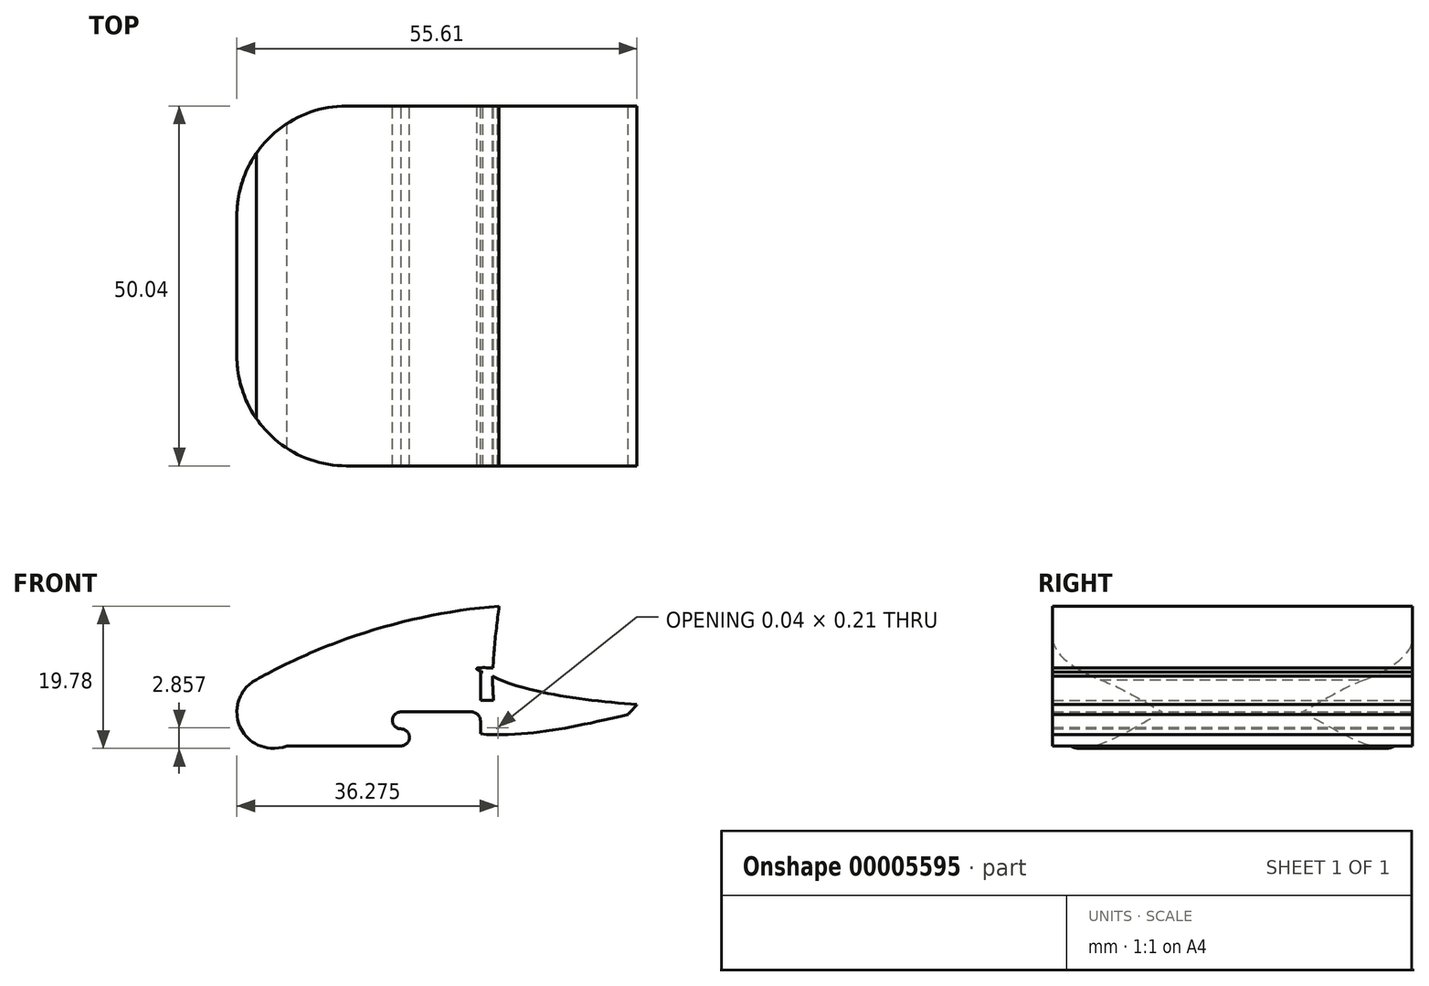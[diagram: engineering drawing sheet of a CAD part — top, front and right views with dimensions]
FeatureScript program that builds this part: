
annotation { "Feature Type Name" : "Feature", "Feature Type Description" : "" }
export const myFeature = defineFeature(function(context is Context, id is Id, definition is map)
    precondition{}
    {
        {
            var Q0;
            Q0=qCreatedBy(makeId("Top.planeOp"),FACE);
            var sketch = newSketch(context, id + "F0", { "sketchPlane" : qUnion([Q0])});
            skLineSegment(sketch, "E0.bottom", {"start": v(-7.57, 33.45) * mm, "end": v(37.92, 33.45) * mm});
            skLineSegment(sketch, "E0.top", {"start": v(-7.57, -16.6) * mm, "end": v(37.92, -16.6) * mm});
            skLineSegment(sketch, "E0.left", {"start": v(-22.81, 18.2) * mm, "end": v(-22.81, -1.35) * mm});
            skLineSegment(sketch, "E0.right", {"start": v(37.92, 33.45) * mm, "end": v(37.92, -16.6) * mm});
            skPoint(sketch, "E1.visualSharp", {"position": v(-22.81, 33.45) * mm});
            skArc(sketch, "E1.filletArc", {"start": v(-7.57, 33.45) * mm, "mid": v(-18.35, 28.98) * mm, "end": v(-22.81, 18.2) * mm});
            skPoint(sketch, "E2.visualSharp", {"position": v(-22.81, -16.6) * mm});
            skArc(sketch, "E2.filletArc", {"start": v(-22.81, -1.35) * mm, "mid": v(-18.35, -12.13) * mm, "end": v(-7.57, -16.6) * mm});
            skSolve(sketch);
        }
        {
            var Q0;
            Q0=qCreatedBy(makeId("Front.planeOp"),FACE);
            var sketch = newSketch(context, id + "F1", { "sketchPlane" : qUnion([Q0])});
            skPoint(sketch, "E3.first.point", {"position": v(-22.81, 0) * mm});
            skPoint(sketch, "E3.second.point", {"position": v(-22.81, 0) * mm});
            skLineSegment(sketch, "E4", {"start": v(-15.88, -4.73) * mm, "end": v(0, -4.73) * mm});
            skLineSegment(sketch, "E5", {"start": v(11.05, -1.27) * mm, "end": v(11.05, -5.54) * mm});
            skFitSpline(sketch, "E6", {"points": [v(11.05, -5.54) * mm, v(29.15, -2.33) * mm, v(36.06, 4.72) * mm], "startDerivative": vector(15.96, -0.07) * mm, "endDerivative": vector(7.94, 0) * mm});
            skArc(sketch, "E7", {"start": v(0, -4.73) * mm, "mid": v(1.18, -3.55) * mm, "end": v(0, -2.37) * mm});
            skArc(sketch, "E8", {"start": v(0, 0) * mm, "mid": v(-1.18, -1.19) * mm, "end": v(0, -2.37) * mm});
            skPoint(sketch, "E9.orphan", {"position": v(0, 0) * mm});
            skPoint(sketch, "E10.trimOffspring.start.orphan", {"position": v(0, -2.37) * mm});
            skLineSegment(sketch, "E11", {"start": v(0, 0) * mm, "end": v(9.78, 0) * mm});
            skPoint(sketch, "E12.visualSharp", {"position": v(11.05, 0) * mm});
            skArc(sketch, "E12.filletArc", {"start": v(11.05, -1.27) * mm, "mid": v(10.68, -0.37) * mm, "end": v(9.78, 0) * mm});
            skArc(sketch, "E13", {"start": v(11.05, -5.54) * mm, "mid": v(12.3, -6.66) * mm, "end": v(13.4, -5.38) * mm});
            skFitSpline(sketch, "E14.0", {"points": [v(8.32, -2.6) * mm, v(10, -2.92) * mm, v(12.5, -3.16) * mm, v(15.86, -3.11) * mm, v(18.41, -2.9) * mm, v(21.02, -2.55) * mm, v(23.71, -2.08) * mm, v(26.5, -1.52) * mm, v(29.4, -0.88) * mm, v(31.71, -0.3) * mm, v(33.4, 0.16) * mm, v(34.56, 0.52) * mm, v(35.58, 0.88) * mm, v(36.43, 1.23) * mm, v(36.97, 1.52) * mm, v(37.28, 1.73) * mm, v(37.44, 1.88) * mm, v(37.53, 2) * mm, v(37.56, 2.05) * mm, v(37.55, 2.05) * mm, v(37.55, 2.08) * mm, v(37.5, 2.16) * mm, v(37.39, 2.27) * mm, v(37.21, 2.4) * mm, v(36.9, 2.56) * mm, v(36.4, 2.76) * mm, v(35.68, 2.95) * mm, v(34.88, 3.08) * mm, v(34.33, 3.1) * mm, v(34.06, 3.11) * mm]});
            skArc(sketch, "E15", {"start": v(37.04, 3.92) * mm, "mid": v(37.04, 3.92) * mm, "end": v(37.04, 3.92) * mm});
            skFitSpline(sketch, "E16", {"points": [v(13.64, -3.12) * mm, v(12.75, 3.68) * mm, v(13.64, 14.7) * mm], "startDerivative": vector(-2.8, 14.5) * mm, "endDerivative": vector(2.58, 20.9) * mm});
            skArc(sketch, "E17", {"start": v(13.64, 14.7) * mm, "mid": v(-3.8, 11.4) * mm, "end": v(-20.13, 4.48) * mm});
            skArc(sketch, "E18", {"start": v(-20.13, 4.48) * mm, "mid": v(-22.34, -2.13) * mm, "end": v(-15.88, -4.73) * mm});
            skArc(sketch, "E19", {"start": v(11.05, -5.44) * mm, "mid": v(12.18, -6.66) * mm, "end": v(13.4, -5.54) * mm});
            skFitSpline(sketch, "E20", {"points": [v(11.05, -5.54) * mm, v(29.15, -2.33) * mm, v(38.07, 2.57) * mm, v(35.95, 3.97) * mm], "startDerivative": vector(15.96, -0.07) * mm, "endDerivative": vector(-27.33, -2.96) * mm});
            skLineSegment(sketch, "E21", {"start": v(11.05, 1.62) * mm, "end": v(11.05, 5.53) * mm, "construction": true});
            skLineSegment(sketch, "E22.bottom", {"start": v(11.05, 1.62) * mm, "end": v(12.88, 1.62) * mm});
            skLineSegment(sketch, "E22.top", {"start": v(11.05, 5.5) * mm, "end": v(12.76, 5.5) * mm});
            skLineSegment(sketch, "E22.left", {"start": v(11.05, 1.62) * mm, "end": v(11.05, 5.5) * mm});
            skFitSpline(sketch, "E23.trimOffspring", {"points": [v(13.64, -3.12) * mm, v(12.75, 3.68) * mm, v(13.64, 14.7) * mm], "startDerivative": vector(-2.8, 14.5) * mm, "endDerivative": vector(2.58, 20.9) * mm});
            skLineSegment(sketch, "E24.top", {"start": v(0, -4.73) * mm, "end": v(-15.8, -4.73) * mm});
            skLineSegment(sketch, "E24.left", {"start": v(11.05, 4.48) * mm, "end": v(11.05, 1.62) * mm});
            skLineSegment(sketch, "E25.bottom", {"start": v(-15.8, -4.73) * mm, "end": v(0, -4.73) * mm});
            skLineSegment(sketch, "E26.right", {"start": v(11.05, 1.62) * mm, "end": v(11.05, 3.58) * mm});
            skLineSegment(sketch, "E27.trimOffspring", {"start": v(0, 0) * mm, "end": v(0, 0) * mm});
            skLineSegment(sketch, "E28.top", {"start": v(13.4, -5.44) * mm, "end": v(13.44, -5.44) * mm});
            skLineSegment(sketch, "E28.left", {"start": v(11.05, -1.27) * mm, "end": v(11.05, -5.44) * mm});
            skLineSegment(sketch, "E28.right", {"start": v(13.44, -2.12) * mm, "end": v(13.44, -2.33) * mm});
            skLineSegment(sketch, "E29.bottom", {"start": v(11.05, -5.54) * mm, "end": v(11.05, -5.54) * mm});
            skLineSegment(sketch, "E29.top", {"start": v(13.44, -2.33) * mm, "end": v(13.48, -2.33) * mm});
            skLineSegment(sketch, "E29.left", {"start": v(11.05, -5.54) * mm, "end": v(11.05, -2.33) * mm});
            skLineSegment(sketch, "E30.trimOffspring", {"start": v(13.44, -5.38) * mm, "end": v(13.44, -5.44) * mm});
            skLineSegment(sketch, "E31.trimOffspring", {"start": v(11.05, -1.27) * mm, "end": v(11.05, -4.73) * mm});
            skArc(sketch, "E32", {"start": v(37.04, 3.92) * mm, "mid": v(36.8, 3.73) * mm, "end": v(36.93, 3.45) * mm});
            skFitSpline(sketch, "E33", {"points": [v(10.58, 6.07) * mm, v(12.08, 5.23) * mm, v(14.38, 4.22) * mm, v(17.59, 3.23) * mm, v(20.08, 2.63) * mm, v(22.67, 2.16) * mm, v(25.37, 1.77) * mm, v(28.2, 1.44) * mm, v(31.15, 1.15) * mm, v(33.53, 0.97) * mm, v(35.28, 0.9) * mm, v(36.5, 0.87) * mm, v(37.58, 0.9) * mm, v(38.5, 0.97) * mm, v(39.1, 1.08) * mm, v(39.45, 1.18) * mm, v(39.65, 1.27) * mm, v(39.78, 1.35) * mm, v(39.82, 1.4) * mm, v(39.81, 1.4) * mm, v(39.82, 1.42) * mm, v(39.8, 1.51) * mm, v(39.72, 1.66) * mm, v(39.6, 1.83) * mm, v(39.35, 2.08) * mm, v(38.94, 2.43) * mm, v(38.31, 2.83) * mm, v(37.6, 3.2) * mm, v(37.08, 3.4) * mm, v(36.82, 3.5) * mm, v(10.58, 6.07) * mm]});
            skFitSpline(sketch, "E34", {"points": [v(35.65, 0.92) * mm, v(37.6, 2.65) * mm, v(36.93, 3.45) * mm, v(35.04, 3.45) * mm], "startDerivative": vector(7.1, 4.46) * mm, "endDerivative": vector(-5.65, -0.87) * mm});
            skSolve(sketch);
        }
        {
            var Q0;
            Q0=makeQuery(id+"F0.imprint","IMPRINT",FACE,{"disambiguationData":[TD([[makeQuery(id+"F0.imprint","IMPRINT",EDGE,{"derivedFrom":sQuery(id+"F0.wireOp",EDGE,"E0.bottom")}),-1.0]])]});
            extrude(context, id + "F2", {"entities" : qUnion([Q0]), "depth" : 31.86 * mm, "symmetric" : true});
        }
        {
            var Q0;
            Q0=makeQuery(id+"F1.imprint","IMPRINT",FACE,{"disambiguationData":[TD([[makeQuery(id+"F1.imprint","IMPRINT",EDGE,{"derivedFrom":sQuery(id+"F1.wireOp",EDGE,"E4")}),1.0]])]});
            extrude(context, id + "F3", {"entities" : qUnion([Q0]), "depth" : 87.36 * mm, "symmetric" : true});
        }
        {
            var Q0;
            Q0=makeQuery(id+"F2.opExtrude","SWEPT_BODY",BODY,{"disambiguationData":[OSD([sQuery(id+"F0.wireOp",EDGE,"E0.bottom"),sQuery(id+"F0.wireOp",EDGE,"E0.top"),sQuery(id+"F0.wireOp",EDGE,"E0.left"),sQuery(id+"F0.wireOp",EDGE,"E0.right"),sQuery(id+"F0.wireOp",EDGE,"E1.filletArc"),sQuery(id+"F0.wireOp",EDGE,"E2.filletArc")])]});
            var Q1;
            Q1=makeQuery(id+"F3.opExtrude","SWEPT_BODY",BODY,{"disambiguationData":[OSD([sQuery(id+"F1.wireOp",EDGE,"E4"),sQuery(id+"F1.wireOp",EDGE,"E5"),sQuery(id+"F1.wireOp",EDGE,"E7"),sQuery(id+"F1.wireOp",EDGE,"E8"),sQuery(id+"F1.wireOp",EDGE,"E12.filletArc"),sQuery(id+"F1.wireOp",EDGE,"E13"),sQuery(id+"F1.wireOp",EDGE,"E14.0"),sQuery(id+"F1.wireOp",EDGE,"E15"),sQuery(id+"F1.wireOp",EDGE,"E16"),sQuery(id+"F1.wireOp",EDGE,"E17"),sQuery(id+"F1.wireOp",EDGE,"E18"),sQuery(id+"F1.wireOp",EDGE,"E19"),sQuery(id+"F1.wireOp",EDGE,"E20"),sQuery(id+"F1.wireOp",EDGE,"E22.top"),sQuery(id+"F1.wireOp",EDGE,"E22.left"),sQuery(id+"F1.wireOp",EDGE,"E23.trimOffspring"),sQuery(id+"F1.wireOp",EDGE,"E24.left"),sQuery(id+"F1.wireOp",EDGE,"E25.bottom"),sQuery(id+"F1.wireOp",EDGE,"E11"),sQuery(id+"F1.wireOp",EDGE,"E26.right"),sQuery(id+"F1.wireOp",EDGE,"E27.trimOffspring"),sQuery(id+"F1.wireOp",EDGE,"E22.bottom"),sQuery(id+"F1.wireOp",EDGE,"E28.top"),sQuery(id+"F1.wireOp",EDGE,"E28.left"),sQuery(id+"F1.wireOp",EDGE,"E28.right"),sQuery(id+"F1.wireOp",EDGE,"E29.top"),sQuery(id+"F1.wireOp",EDGE,"E30.trimOffspring"),sQuery(id+"F1.wireOp",EDGE,"E31.trimOffspring"),sQuery(id+"F1.wireOp",EDGE,"E32"),sQuery(id+"F1.wireOp",EDGE,"E34")])]});
            booleanBodies(context, id + "F4", {"operationType" : BooleanOperationType.INTERSECTION, "tools" : qUnion([Q0, Q1])});
        }
    });
